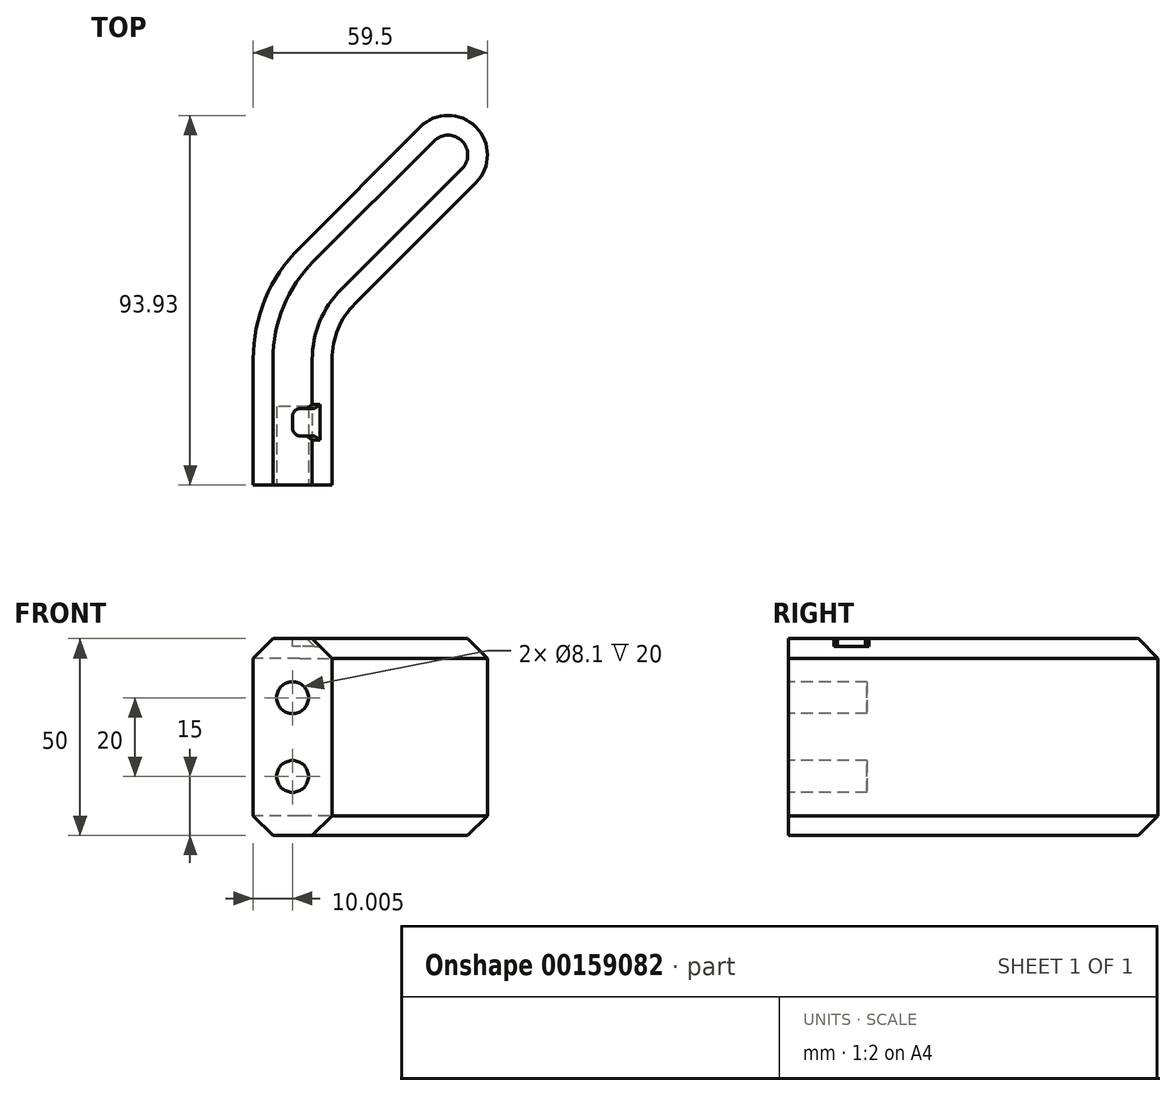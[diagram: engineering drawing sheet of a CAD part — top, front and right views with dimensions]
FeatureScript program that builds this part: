
annotation { "Feature Type Name" : "Feature", "Feature Type Description" : "" }
export const myFeature = defineFeature(function(context is Context, id is Id, definition is map)
    precondition{}
    {
        {
            var Q0;
            Q0=qCreatedBy(makeId("Top.planeOp"),FACE);
            var sketch = newSketch(context, id + "F0", { "sketchPlane" : qUnion([Q0])});
            skLineSegment(sketch, "E0", {"start": v(11.73, 60.4) * mm, "end": v(42.44, 91.1) * mm});
            skLineSegment(sketch, "E1", {"start": v(56.58, 76.97) * mm, "end": v(25.87, 46.26) * mm});
            skLineSegment(sketch, "E2", {"start": v(20.01, 32.11) * mm, "end": v(20.01, 0.11) * mm});
            skLineSegment(sketch, "E3", {"start": v(0.01, 32.11) * mm, "end": v(0.01, 0.11) * mm});
            skPoint(sketch, "E4.visualSharp", {"position": v(20.01, 40.4) * mm});
            skArc(sketch, "E4.filletArc", {"start": v(25.87, 46.26) * mm, "mid": v(21.54, 39.77) * mm, "end": v(20.01, 32.11) * mm});
            skPoint(sketch, "E5.visualSharp", {"position": v(0.01, 48.68) * mm});
            skArc(sketch, "E5.filletArc", {"start": v(11.73, 60.4) * mm, "mid": v(3.06, 47.42) * mm, "end": v(0.01, 32.11) * mm});
            skArc(sketch, "E6", {"start": v(42.44, 91.1) * mm, "mid": v(56.58, 91.1) * mm, "end": v(56.58, 76.97) * mm});
            skLineSegment(sketch, "E7", {"start": v(0.01, 0.11) * mm, "end": v(20.01, 0.11) * mm});
            skSolve(sketch);
        }
        {
            var Q0;
            Q0=qSketchRegion(id+"F0",true);
            extrude(context, id + "F1", {"entities" : qUnion([Q0]), "depth" : 25 * mm, "hasSecondDirection" : true, "secondDirectionOppositeDirection" : true, "secondDirectionDepth" : 25 * mm});
        }
        {
            var Q0;
            Q0=makeQuery(id+"F1.opExtrude","CAP_EDGE",EDGE,{"disambiguationData":[OSD([sQuery(id+"F0.wireOp",EDGE,"E3")])],"isStart":false});
            var Q1;
            Q1=makeQuery(id+"F1.opExtrude","CAP_EDGE",EDGE,{"disambiguationData":[OSD([sQuery(id+"F0.wireOp",EDGE,"E5.filletArc")])],"isStart":false});
            var Q2;
            Q2=makeQuery(id+"F1.opExtrude","CAP_EDGE",EDGE,{"disambiguationData":[OSD([sQuery(id+"F0.wireOp",EDGE,"E0")])],"isStart":false});
            var Q3;
            Q3=makeQuery(id+"F1.opExtrude","CAP_EDGE",EDGE,{"disambiguationData":[OSD([sQuery(id+"F0.wireOp",EDGE,"E6")])],"isStart":false});
            var Q4;
            Q4=makeQuery(id+"F1.opExtrude","CAP_EDGE",EDGE,{"disambiguationData":[OSD([sQuery(id+"F0.wireOp",EDGE,"E1")])],"isStart":false});
            var Q5;
            Q5=makeQuery(id+"F1.opExtrude","CAP_EDGE",EDGE,{"disambiguationData":[OSD([sQuery(id+"F0.wireOp",EDGE,"E4.filletArc")])],"isStart":false});
            var Q6;
            Q6=makeQuery(id+"F1.opExtrude","CAP_EDGE",EDGE,{"disambiguationData":[OSD([sQuery(id+"F0.wireOp",EDGE,"E2")])],"isStart":false});
            var Q7;
            Q7=makeQuery(id+"F1.opExtrude","CAP_EDGE",EDGE,{"disambiguationData":[OSD([sQuery(id+"F0.wireOp",EDGE,"E1")])],"isStart":true});
            var Q8;
            Q8=makeQuery(id+"F1.opExtrude","CAP_EDGE",EDGE,{"disambiguationData":[OSD([sQuery(id+"F0.wireOp",EDGE,"E6")])],"isStart":true});
            var Q9;
            Q9=makeQuery(id+"F1.opExtrude","CAP_EDGE",EDGE,{"disambiguationData":[OSD([sQuery(id+"F0.wireOp",EDGE,"E0")])],"isStart":true});
            var Q10;
            Q10=makeQuery(id+"F1.opExtrude","CAP_EDGE",EDGE,{"disambiguationData":[OSD([sQuery(id+"F0.wireOp",EDGE,"E5.filletArc")])],"isStart":true});
            var Q11;
            Q11=makeQuery(id+"F1.opExtrude","CAP_EDGE",EDGE,{"disambiguationData":[OSD([sQuery(id+"F0.wireOp",EDGE,"E3")])],"isStart":true});
            var Q12;
            Q12=makeQuery(id+"F1.opExtrude","CAP_EDGE",EDGE,{"disambiguationData":[OSD([sQuery(id+"F0.wireOp",EDGE,"E4.filletArc")])],"isStart":true});
            var Q13;
            Q13=makeQuery(id+"F1.opExtrude","CAP_EDGE",EDGE,{"disambiguationData":[OSD([sQuery(id+"F0.wireOp",EDGE,"E2")])],"isStart":true});
            chamfer(context, id + "F2", {"entities" : qUnion([Q0, Q1, Q2, Q3, Q4, Q5, Q6, Q7, Q8, Q9, Q10, Q11, Q12, Q13]), "width" : 5 * mm, "tangentPropagation" : true});
        }
        {
            var Q0;
            Q0=makeQuery(id+"F1.opExtrude","SWEPT_FACE",FACE,{"disambiguationData":[OSD([sQuery(id+"F0.wireOp",EDGE,"E7")])]});
            var sketch = newSketch(context, id + "F3", { "sketchPlane" : qUnion([Q0])});
            skCircle(sketch, "E8", {"center": v(10.01, 10) * mm, "radius": 4.05 * mm});
            skCircle(sketch, "E9", {"center": v(10.01, -10) * mm, "radius": 4.05 * mm});
            skLineSegment(sketch, "E10", {"start": v(0.01, 0) * mm, "end": v(20.01, 0) * mm, "construction": true});
            skPoint(sketch, "E11", {"position": v(10.01, 0) * mm});
            skSolve(sketch);
        }
        {
            var Q0;
            Q0 = qSketchRegion(id + "F3", true);
            extrude(context, id + "F4", {"entities" : qUnion([Q0]), "operationType" : NewBodyOperationType.REMOVE, "oppositeDirection" : true, "depth" : 20 * mm});
        }
        {
            var Q0;
            Q0=makeQuery(id+"F1.opExtrude","CAP_FACE",FACE,{"disambiguationData":[OSD([sQuery(id+"F0.wireOp",EDGE,"E0"),sQuery(id+"F0.wireOp",EDGE,"E1"),sQuery(id+"F0.wireOp",EDGE,"E2"),sQuery(id+"F0.wireOp",EDGE,"E3"),sQuery(id+"F0.wireOp",EDGE,"E4.filletArc"),sQuery(id+"F0.wireOp",EDGE,"E5.filletArc"),sQuery(id+"F0.wireOp",EDGE,"E6"),sQuery(id+"F0.wireOp",EDGE,"E7")])],"isStart":false});
            var sketch = newSketch(context, id + "F5", { "sketchPlane" : qUnion([Q0])});
            skLineSegment(sketch, "E12.bottom", {"start": v(20.01, 12.61) * mm, "end": v(12.01, 12.61) * mm});
            skLineSegment(sketch, "E12.top", {"start": v(20.01, 19.61) * mm, "end": v(12.01, 19.61) * mm});
            skLineSegment(sketch, "E12.left", {"start": v(20.01, 12.61) * mm, "end": v(20.01, 19.61) * mm});
            skLineSegment(sketch, "E12.right", {"start": v(10.01, 14.61) * mm, "end": v(10.01, 17.61) * mm});
            skPoint(sketch, "E12.middle", {"position": v(15.01, 16.11) * mm});
            skPoint(sketch, "E13.visualSharp", {"position": v(10.01, 19.61) * mm});
            skArc(sketch, "E13.filletArc", {"start": v(12.01, 19.61) * mm, "mid": v(10.6, 19.03) * mm, "end": v(10.01, 17.61) * mm});
            skPoint(sketch, "E14.visualSharp", {"position": v(10.01, 12.61) * mm});
            skArc(sketch, "E14.filletArc", {"start": v(10.01, 14.61) * mm, "mid": v(10.6, 13.2) * mm, "end": v(12.01, 12.61) * mm});
            skSolve(sketch);
        }
        {
            var Q0;
            Q0 = qSketchRegion(id + "F5", true);
            extrude(context, id + "F6", {"entities" : qUnion([Q0]), "operationType" : NewBodyOperationType.REMOVE, "oppositeDirection" : true, "depth" : 2 * mm});
        }
        {
            var Q0;
            Q0=makeQuery(id+"F6.boolean.opBoolean","COPY",EDGE,{"derivedFrom":makeQuery(id+"F6.opExtrude","CAP_EDGE",EDGE,{"disambiguationData":[OSD([sQuery(id+"F5.wireOp",EDGE,"E13.filletArc")])],"isStart":true})});
            var Q1;
            Q1=makeQuery(id+"F6.boolean.opBoolean","COPY",EDGE,{"derivedFrom":makeQuery(id+"F6.opExtrude","CAP_EDGE",EDGE,{"disambiguationData":[OSD([sQuery(id+"F5.wireOp",EDGE,"E12.right")])],"isStart":true})});
            var Q2;
            Q2=makeQuery(id+"F6.boolean.opBoolean","COPY",EDGE,{"derivedFrom":makeQuery(id+"F6.opExtrude","CAP_EDGE",EDGE,{"disambiguationData":[OSD([sQuery(id+"F5.wireOp",EDGE,"E14.filletArc")])],"isStart":true})});
            var Q3;
            Q3=makeQuery(id+"F6.boolean.opBoolean","COPY",EDGE,{"derivedFrom":makeQuery(id+"F6.opExtrude","CAP_EDGE",EDGE,{"disambiguationData":[OSD([sQuery(id+"F5.wireOp",EDGE,"E12.bottom")])],"isStart":true})});
            var Q4;
            {var subQ0=sQuery(id+"F0.wireOp",EDGE,"E2");Q4=makeQuery(id+"F6.boolean.opBoolean","INTERSECT",EDGE,{"derivedFrom":[makeQuery(id+"F2.opChamfer","BLEND_FACE",FACE,{"disambiguationData":[OSD([subQ0]),TDD([makeQuery(id+"F1.opExtrude","CAP_EDGE",EDGE,{"disambiguationData":[OSD([subQ0])],"isStart":false})])]}),makeQuery(id+"F6.opExtrude","SWEPT_FACE",FACE,{"disambiguationData":[OSD([sQuery(id+"F5.wireOp",EDGE,"E12.bottom")])]})]});}
            var Q5;
            Q5=makeQuery(id+"F6.boolean.opBoolean","COPY",EDGE,{"derivedFrom":makeQuery(id+"F6.opExtrude","CAP_EDGE",EDGE,{"disambiguationData":[OSD([sQuery(id+"F5.wireOp",EDGE,"E12.top")])],"isStart":true})});
            var Q6;
            {var subQ0=sQuery(id+"F0.wireOp",EDGE,"E2");Q6=makeQuery(id+"F6.boolean.opBoolean","INTERSECT",EDGE,{"derivedFrom":[makeQuery(id+"F2.opChamfer","BLEND_FACE",FACE,{"disambiguationData":[OSD([subQ0]),TDD([makeQuery(id+"F1.opExtrude","CAP_EDGE",EDGE,{"disambiguationData":[OSD([subQ0])],"isStart":false})])]}),makeQuery(id+"F6.opExtrude","SWEPT_FACE",FACE,{"disambiguationData":[OSD([sQuery(id+"F5.wireOp",EDGE,"E12.top")])]})]});}
            chamfer(context, id + "F7", {"entities" : qUnion([Q0, Q1, Q2, Q3, Q4, Q5, Q6]), "width" : 1 * mm, "tangentPropagation" : true});
        }
    });
